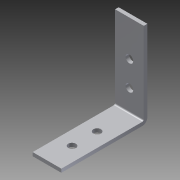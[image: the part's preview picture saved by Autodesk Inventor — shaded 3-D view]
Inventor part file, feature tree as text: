
AUTODESK INVENTOR PART (.ipt)
format: ipt  version: 2014 SP1 (Build 180222100, 222)  size: 161,792 bytes
history: native  units: in
note: dims shown in document units (in); Inventor stores cm internally (conversion verified against a paired STEP export)
features: other x4, sheet_metal_op x3, sketch x3
ambient origin geometry x8: Origin, YZ Plane, XZ Plane, XY Plane, X Axis, Y Axis, Z Axis, Center Point
bodies: Solid1 (feature_tree)
feature tree (10):
  sheet_metal_op  "Face1"
  sheet_metal_op  "Flange1"
  sketch  "Sketch1"  dims[d0=3.0in]
  other  "Plate1"
  sketch  "Sketch2"  dims[d1=1.0in]
  other  "Plate2"
  sheet_metal_op  "Bend1"
  sketch  "Sketch3"  dims[d3=0.266in d4=0.875in d8=0.266in d10=0.125in d11=0.125in d12=0.0625in d13=0.25in d14=0.125in d15=3.0in d16=90.0deg d17=0.05in d18=0.5in d19=0.125in d20=0.125in d21=0.266in d22=0.266in d23=0.5in d24=0.875in d25=0.875in d26=0.125in d27=0.0in d2=0.25in d5=0.25in d6=0.125in d7=0.0in]
  other  "Cut1"
  other  "Definition1"
